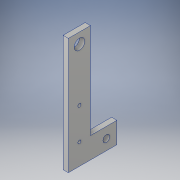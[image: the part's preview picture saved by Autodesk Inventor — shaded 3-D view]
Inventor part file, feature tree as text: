
AUTODESK INVENTOR PART (.ipt)
format: ipt  version: 2019 (Build 230136000, 136)  size: 123,392 bytes
history: native  units: in
note: dims shown in document units (in); Inventor stores cm internally (conversion verified against a paired STEP export)
features: sketch x2, extrude x1, hole x1
ambient origin geometry x8: Origin, YZ Plane, XZ Plane, XY Plane, X Axis, Y Axis, Z Axis, Center Point
bodies: Solid1 (feature_tree)
feature tree (4):
  extrude  "Extrusion1"  Depth=5.5in
  hole  "Hole1"  [1 undecoded]
  sketch  "Sketch1"  dims[d0=5.5in d2=0.5in]
  sketch  "Sketch2"  dims[d3=0.32in d5=4.5in d6=0.5in d7=0.5in d8=0.522in d9=0.5in d10=0.25in d11=0.0in d12=2.5in d13=1.0in d14=1.044in d15=0.522in d16=0.522in d17=0.15in d18=0.75in d19=0.375in d20=0.25in d21=0.5635in d22=1.0in d23=0.8108in d24=1.044in d26=1.272in]
note: 1 required parameter value undecoded (feature->parameter linkage not recoverable at this tier; creation-order binding heuristic only, values carry confidence <= 0.55)
